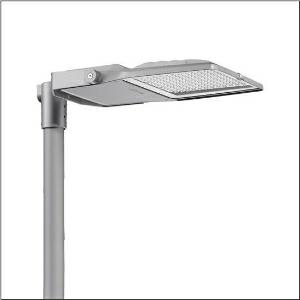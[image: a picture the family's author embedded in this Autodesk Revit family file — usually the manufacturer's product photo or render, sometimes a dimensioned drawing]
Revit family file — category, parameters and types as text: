
# Revit family: floodlight_fl_21_midi___pl64_5xa7786e2e3a_c0a1
name_source: partatom
category: Lighting Fixtures
units: mm (PartAtom-declared; Revit-internal decimal feet)

## family parameters
Cut with Voids When Loaded = No
Host = Face
Light Source = No
Part Type = Normal
Room Calculation Point = No
Round Connector Dimension = Use Diameter
Shared = No

## types (1)
- --- (1 x LED, 26020 lm, 212.4 W, 3000K)
    Apparent Load = 212 VA
    CIE Flux Codes = 28 80 98 100 100
    Color Rendering = 70
    Color Temperature = 3000K
    Default Elevation = 1800 mm
    Description = Floodlight FL 21 midi, floodlight, primary light control with lens, of PMMA, primary optical cover: protective disc, of toughened safety glass, transparent, light distribution: PL64, light emission: direct distribution, installation type: surface-mounted, LED, High Power LED, rated luminous flux: 26.020lm, luminous efficacy: 123lm/W, light colour: 730, colour temperature: 3000K, control gear: Smart Interface (Zhaga), control: flexible luminous flux parameterisation, time-dependent luminous flux control, constant luminous flux control, overheat protection, pre-setting: logarithmic dimming characteristic, with terminal, 6-pole, mains connection: 220..240V, AC, 50/60Hz, start of lifetime: 212W, end of service life: 231W, reduction: 95W, luminaire housing, of diecast aluminium, powder-coated, SITECO metallic grey (DB 702S), corrosivity category C5 mid according to DIN EN ISO 12944, suitable for swimming pools, chlorine-resistant, sealing non-destructively replaceable, please order mast flange separately, mast bracket, of steel, galvanised, powder-coated, SITECO metallic grey (DB 702S), Smart Interface below and above, protection rating (complete): IP66, insulation class (complete): insulation class II (safety insulation), certification: CE, ENEC, VDE, protection symbol: D, impact resistance: IK08, permissible operating ambient temperature: -40..+40°C, permissible operating ambient temperature for outdoor applications: -40..+50°C, standard: DIN EN 12944, LABS conformity tested according to VDMA 24364:2018-05, packaging unit: 1 piece

Light Distribution: PL64
    Height = 76 mm
    Lamp = 1 x LED
    Lamp Light Flux = 26020 lm
    Lamp Power = 212.4 W
    Lamp count = 1
    Length = 657 mm
    Luminous efficacy = 123 lm/W
    Manufacturer = Siteco
    ModVariant = No
    Model = 5XA7786E2E3A
    Number of Poles = 1
    OnlyDefault = Yes
    Power Factor = 1
    Product Name = Floodlight FL 21 midi | PL64
    Product group = floodlight | pylon annexe
    ProductGroupID = 6201
    Protection Class = Protection class II
    Protection Degree = IP 66
    RLX_Detail_Level = 1
    RLX_Emergency_Light_Flux = 0 lm
    RLX_Emergency_Type = 0
    RLX_Emergency_Type_DB = No
    RlxData = <blob elided: 153553 chars, md5=b355a485>
    Socket = socket
    Standby Power = 0 W
    System Light Flux = 26020 lm
    System Power = 212 W
    Type Comments = factory setting: luminous flux: 100 % | dim-lin: 254 | 710 mA
    Type Image = l_1007123.jpg
    URL = http://relux.com
    VarID = @adj_179085
    Voltage = 0 V
    Weight = 0.00 kg
    Width = 442 mm

## geometry (parser evidence)
native form markers: Blend x4, Sweep x15
no freeform markers — native parametric forms only
